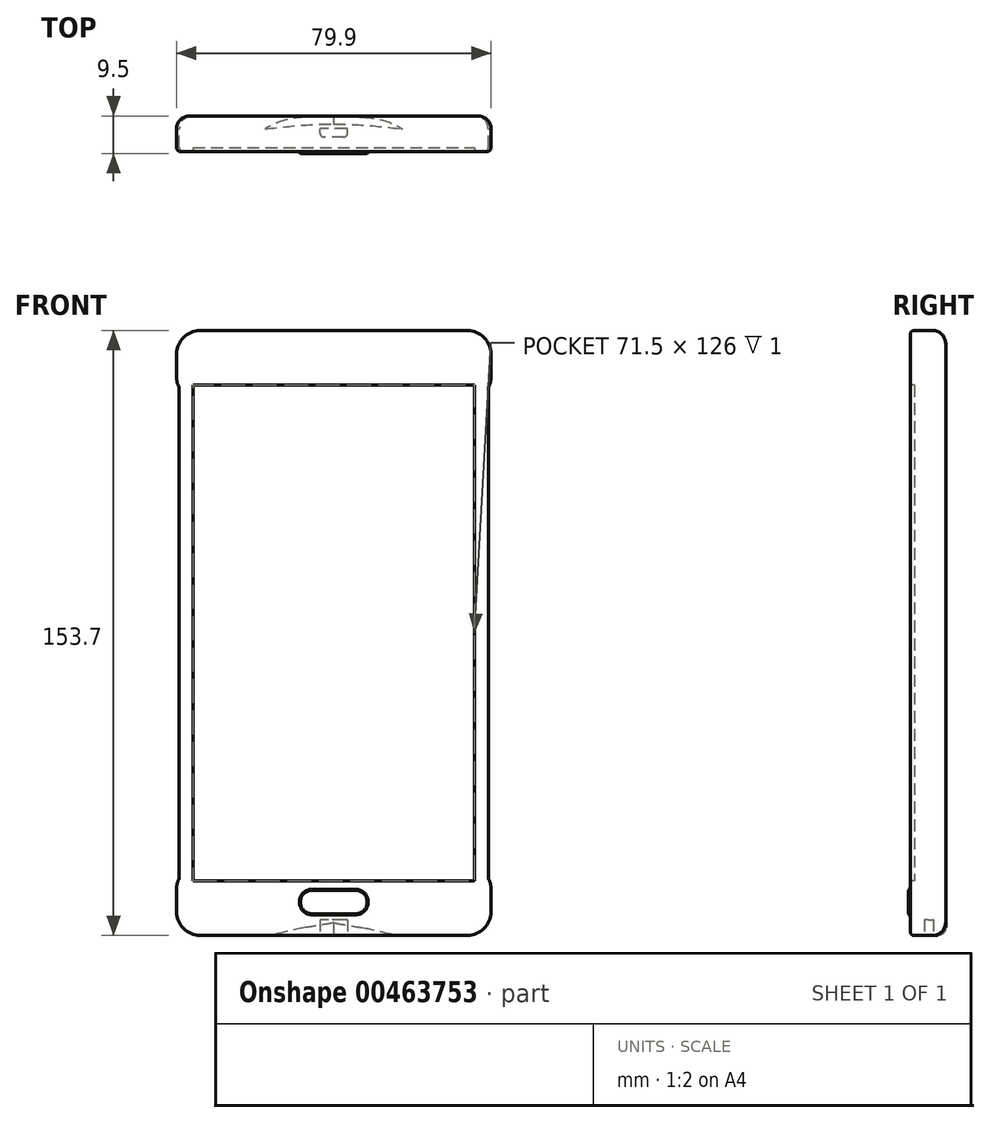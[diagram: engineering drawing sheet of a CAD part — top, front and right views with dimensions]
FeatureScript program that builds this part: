
annotation { "Feature Type Name" : "Feature", "Feature Type Description" : "" }
export const myFeature = defineFeature(function(context is Context, id is Id, definition is map)
    precondition{}
    {
        {
            var Q0;
            Q0=qCreatedBy(makeId("Front.planeOp"),FACE);
            var sketch = newSketch(context, id + "F0", { "sketchPlane" : qUnion([Q0])});
            skLineSegment(sketch, "E0.bottom", {"start": v(33.25, 76.85) * mm, "end": v(-33.25, 76.85) * mm});
            skLineSegment(sketch, "E0.top", {"start": v(33.95, -76.85) * mm, "end": v(-33.95, -76.85) * mm});
            skLineSegment(sketch, "E0.left", {"start": v(39.25, 61.9) * mm, "end": v(39.25, -61.9) * mm});
            skLineSegment(sketch, "E0.right", {"start": v(-39.25, 61.9) * mm, "end": v(-39.25, -61.9) * mm});
            skPoint(sketch, "E0.middle", {"position": v(0, 0) * mm});
            skLineSegment(sketch, "E1", {"start": v(0, 76.85) * mm, "end": v(0, -76.85) * mm, "construction": true});
            skLineSegment(sketch, "E2", {"start": v(-39.25, 0) * mm, "end": v(39.25, 0) * mm, "construction": true});
            skPoint(sketch, "E3.visualSharp", {"position": v(-39.25, 76.85) * mm});
            skPoint(sketch, "E4.visualSharp", {"position": v(39.25, 76.85) * mm});
            skPoint(sketch, "E5.visualSharp", {"position": v(39.25, -76.85) * mm});
            skPoint(sketch, "E6.visualSharp", {"position": v(-39.25, -76.85) * mm});
            skLineSegment(sketch, "E7.0", {"start": v(33.25, -62.85) * mm, "end": v(0, -62.85) * mm, "construction": true});
            skLineSegment(sketch, "E8.0", {"start": v(-39.95, -64.95) * mm, "end": v(-39.95, -70.85) * mm});
            skPoint(sketch, "E9.visualSharp", {"position": v(-39.95, -76.85) * mm});
            skArc(sketch, "E9.filletArc", {"start": v(-39.95, -70.85) * mm, "mid": v(-38.2, -75.1) * mm, "end": v(-33.95, -76.85) * mm});
            skPoint(sketch, "E10.visualSharp", {"position": v(-39.25, -62.85) * mm});
            skArc(sketch, "E10.filletArc", {"start": v(-39.45, -62.77) * mm, "mid": v(-39.3, -62.34) * mm, "end": v(-39.25, -61.9) * mm});
            skPoint(sketch, "E11.visualSharp", {"position": v(-39.95, -63.42) * mm});
            skArc(sketch, "E11.filletArc", {"start": v(-39.45, -62.77) * mm, "mid": v(-39.82, -63.83) * mm, "end": v(-39.95, -64.95) * mm});
            skArc(sketch, "E12.MirrorCS", {"start": v(39.45, -62.77) * mm, "mid": v(39.3, -62.34) * mm, "end": v(39.25, -61.9) * mm});
            skPoint(sketch, "E13.MirrorP", {"position": v(39.95, -63.42) * mm});
            skLineSegment(sketch, "E14.MirrorCS", {"start": v(39.95, -64.95) * mm, "end": v(39.95, -70.85) * mm});
            skArc(sketch, "E15.MirrorCS", {"start": v(39.95, -70.85) * mm, "mid": v(38.2, -75.1) * mm, "end": v(33.95, -76.85) * mm});
            skArc(sketch, "E16.MirrorCS", {"start": v(39.45, -62.77) * mm, "mid": v(39.82, -63.83) * mm, "end": v(39.95, -64.95) * mm});
            skArc(sketch, "E17.MirrorCS", {"start": v(39.45, 62.77) * mm, "mid": v(39.3, 62.34) * mm, "end": v(39.25, 61.9) * mm});
            skArc(sketch, "E18.MirrorCS", {"start": v(-39.45, 62.77) * mm, "mid": v(-39.3, 62.34) * mm, "end": v(-39.25, 61.9) * mm});
            skArc(sketch, "E19.MirrorCS", {"start": v(39.45, 62.77) * mm, "mid": v(39.82, 63.83) * mm, "end": v(39.95, 64.95) * mm});
            skArc(sketch, "E20.MirrorCS", {"start": v(-39.45, 62.77) * mm, "mid": v(-39.82, 63.83) * mm, "end": v(-39.95, 64.95) * mm});
            skArc(sketch, "E21.MirrorCS", {"start": v(39.95, 70.85) * mm, "mid": v(38.2, 75.1) * mm, "end": v(33.95, 76.85) * mm});
            skLineSegment(sketch, "E22.MirrorCS", {"start": v(39.95, 64.95) * mm, "end": v(39.95, 70.85) * mm});
            skArc(sketch, "E23.MirrorCS", {"start": v(-39.95, 70.85) * mm, "mid": v(-38.2, 75.1) * mm, "end": v(-33.95, 76.85) * mm});
            skLineSegment(sketch, "E24.MirrorCS", {"start": v(-39.95, 64.95) * mm, "end": v(-39.95, 70.85) * mm});
            skPoint(sketch, "E25.MirrorP", {"position": v(-39.95, 76.85) * mm});
            skPoint(sketch, "E26.MirrorP", {"position": v(-39.25, 62.85) * mm});
            skLineSegment(sketch, "E27.MirrorCS", {"start": v(33.25, 62.85) * mm, "end": v(0, 62.85) * mm, "construction": true});
            skPoint(sketch, "E28.MirrorP", {"position": v(-39.95, 63.42) * mm});
            skLineSegment(sketch, "E29.MirrorCS", {"start": v(33.95, 76.85) * mm, "end": v(-33.95, 76.85) * mm});
            skPoint(sketch, "E30.MirrorP", {"position": v(39.95, 63.42) * mm});
            skSolve(sketch);
        }
        {
            var Q0;
            Q0=makeQuery(id+"F0.imprint","IMPRINT",FACE,{"disambiguationData":[TD([[makeQuery(id+"F0.imprint","IMPRINT",EDGE,{"derivedFrom":sQuery(id+"F0.wireOp",EDGE,"E0.top")}),-1.0]])]});
            extrude(context, id + "F1", {"entities" : qUnion([Q0]), "depth" : 9 * mm});
        }
        {
            var Q0;
            Q0=makeQuery(id+"F1.opExtrude","CAP_FACE",FACE,{"disambiguationData":[OSD([sQuery(id+"F0.wireOp",EDGE,"E0.bottom"),sQuery(id+"F0.wireOp",EDGE,"E0.top"),sQuery(id+"F0.wireOp",EDGE,"E0.left"),sQuery(id+"F0.wireOp",EDGE,"E0.right"),sQuery(id+"F0.wireOp",EDGE,"E3.filletArc"),sQuery(id+"F0.wireOp",EDGE,"E4.filletArc"),sQuery(id+"F0.wireOp",EDGE,"E5.filletArc"),sQuery(id+"F0.wireOp",EDGE,"E6.filletArc")])],"isStart":false});
            var sketch = newSketch(context, id + "F2", { "sketchPlane" : qUnion([Q0])});
            skLineSegment(sketch, "E31.0", {"start": v(33.5, -68.35) * mm, "end": v(-33.5, -68.35) * mm, "construction": true});
            skLineSegment(sketch, "E32.0", {"start": v(0, 76.85) * mm, "end": v(0, -76.85) * mm, "construction": true});
            skLineSegment(sketch, "E33.bottom", {"start": v(5.5, -65.1) * mm, "end": v(-5.5, -65.1) * mm});
            skLineSegment(sketch, "E33.top", {"start": v(5.5, -71.6) * mm, "end": v(-5.5, -71.6) * mm});
            skLineSegment(sketch, "E33.left", {"start": v(8.75, -68.35) * mm, "end": v(8.75, -68.35) * mm});
            skLineSegment(sketch, "E33.right", {"start": v(-8.75, -68.35) * mm, "end": v(-8.75, -68.35) * mm});
            skPoint(sketch, "E33.middle", {"position": v(0, -68.35) * mm});
            skPoint(sketch, "E34.visualSharp", {"position": v(8.75, -65.1) * mm});
            skArc(sketch, "E34.filletArc", {"start": v(8.75, -68.35) * mm, "mid": v(7.8, -66.05) * mm, "end": v(5.5, -65.1) * mm});
            skPoint(sketch, "E35.visualSharp", {"position": v(8.75, -71.6) * mm});
            skArc(sketch, "E35.filletArc", {"start": v(5.5, -71.6) * mm, "mid": v(7.8, -70.65) * mm, "end": v(8.75, -68.35) * mm});
            skPoint(sketch, "E36.visualSharp", {"position": v(-8.75, -71.6) * mm});
            skArc(sketch, "E36.filletArc", {"start": v(-8.75, -68.35) * mm, "mid": v(-7.8, -70.65) * mm, "end": v(-5.5, -71.6) * mm});
            skPoint(sketch, "E37.visualSharp", {"position": v(-8.75, -65.1) * mm});
            skArc(sketch, "E37.filletArc", {"start": v(-5.5, -65.1) * mm, "mid": v(-7.8, -66.05) * mm, "end": v(-8.75, -68.35) * mm});
            skSolve(sketch);
        }
        {
            var Q0;
            Q0=makeQuery(id+"F2.imprint","IMPRINT",FACE,{"disambiguationData":[TD([[makeQuery(id+"F2.imprint","IMPRINT",EDGE,{"derivedFrom":sQuery(id+"F2.wireOp",EDGE,"E33.bottom")}),1.0]])]});
            extrude(context, id + "F3", {"entities" : qUnion([Q0]), "operationType" : NewBodyOperationType.ADD, "depth" : 0.5 * mm});
        }
        {
            var Q0;
            Q0=makeQuery(id+"F3.opExtrude","CAP_EDGE",EDGE,{"disambiguationData":[OSD([sQuery(id+"F2.wireOp",EDGE,"E33.bottom")])],"isStart":false});
            var Q1;
            Q1=makeQuery(id+"F3.opExtrude","CAP_EDGE",EDGE,{"disambiguationData":[OSD([sQuery(id+"F2.wireOp",EDGE,"E34.filletArc"),sQuery(id+"F2.wireOp",EDGE,"E35.filletArc")])],"isStart":false});
            var Q2;
            Q2=makeQuery(id+"F3.opExtrude","CAP_EDGE",EDGE,{"disambiguationData":[OSD([sQuery(id+"F2.wireOp",EDGE,"E33.top")])],"isStart":false});
            var Q3;
            Q3=makeQuery(id+"F3.opExtrude","CAP_EDGE",EDGE,{"disambiguationData":[OSD([sQuery(id+"F2.wireOp",EDGE,"E36.filletArc"),sQuery(id+"F2.wireOp",EDGE,"E37.filletArc")])],"isStart":false});
            chamfer(context, id + "F4", {"entities" : qUnion([Q0, Q1, Q2, Q3]), "width" : 0.25 * mm, "tangentPropagation" : true});
        }
        {
            var Q0;
            Q0=makeQuery(id+"F1.opExtrude","SWEPT_FACE",FACE,{"disambiguationData":[OSD([sQuery(id+"F0.wireOp",EDGE,"E0.top")])]});
            var sketch = newSketch(context, id + "F5", { "sketchPlane" : qUnion([Q0])});
            skLineSegment(sketch, "E38.0", {"start": v(33.95, 3.3) * mm, "end": v(-33.95, 3.3) * mm, "construction": true});
            skSolve(sketch);
        }
        {
            var Q0;
            Q0=makeQuery(id+"F1.opExtrude","CAP_EDGE",EDGE,{"disambiguationData":[OSD([sQuery(id+"F0.wireOp",EDGE,"E0.top")])],"isStart":true});
            fillet(context, id + "F6", {"entities" : qUnion([Q0]), "radius" : 3.3 * mm, "tangentPropagation" : true, "allowEdgeOverflow" : false});
        }
        {
            var Q0;
            Q0=makeQuery(id+"F1.opExtrude","CAP_EDGE",EDGE,{"disambiguationData":[OSD([sQuery(id+"F0.wireOp",EDGE,"E0.left")])],"isStart":false});
            var Q1;
            Q1=makeQuery(id+"F1.opExtrude","CAP_EDGE",EDGE,{"disambiguationData":[OSD([sQuery(id+"F0.wireOp",EDGE,"E0.top")])],"isStart":false});
            var Q2;
            Q2=makeQuery(id+"F1.opExtrude","CAP_EDGE",EDGE,{"disambiguationData":[OSD([sQuery(id+"F0.wireOp",EDGE,"E15.MirrorCS")])],"isStart":false});
            var Q3;
            Q3=makeQuery(id+"F1.opExtrude","CAP_EDGE",EDGE,{"disambiguationData":[OSD([sQuery(id+"F0.wireOp",EDGE,"E14.MirrorCS")])],"isStart":false});
            var Q4;
            Q4=makeQuery(id+"F1.opExtrude","CAP_EDGE",EDGE,{"disambiguationData":[OSD([sQuery(id+"F0.wireOp",EDGE,"E16.MirrorCS")])],"isStart":false});
            var Q5;
            Q5=makeQuery(id+"F1.opExtrude","CAP_EDGE",EDGE,{"disambiguationData":[OSD([sQuery(id+"F0.wireOp",EDGE,"E12.MirrorCS")])],"isStart":false});
            var Q6;
            Q6=makeQuery(id+"F1.opExtrude","CAP_EDGE",EDGE,{"disambiguationData":[OSD([sQuery(id+"F0.wireOp",EDGE,"E9.filletArc")])],"isStart":false});
            var Q7;
            Q7=makeQuery(id+"F1.opExtrude","CAP_EDGE",EDGE,{"disambiguationData":[OSD([sQuery(id+"F0.wireOp",EDGE,"E0.right")])],"isStart":false});
            var Q8;
            Q8=makeQuery(id+"F1.opExtrude","CAP_EDGE",EDGE,{"disambiguationData":[OSD([sQuery(id+"F0.wireOp",EDGE,"E10.filletArc")])],"isStart":false});
            var Q9;
            Q9=makeQuery(id+"F1.opExtrude","CAP_EDGE",EDGE,{"disambiguationData":[OSD([sQuery(id+"F0.wireOp",EDGE,"E8.0")])],"isStart":false});
            var Q10;
            Q10=makeQuery(id+"F1.opExtrude","CAP_EDGE",EDGE,{"disambiguationData":[OSD([sQuery(id+"F0.wireOp",EDGE,"E11.filletArc")])],"isStart":false});
            var Q11;
            Q11=makeQuery(id+"F1.opExtrude","CAP_FACE",FACE,{"disambiguationData":[OSD([sQuery(id+"F0.wireOp",EDGE,"E0.top"),sQuery(id+"F0.wireOp",EDGE,"E0.left"),sQuery(id+"F0.wireOp",EDGE,"E0.right"),sQuery(id+"F0.wireOp",EDGE,"E8.0"),sQuery(id+"F0.wireOp",EDGE,"E9.filletArc"),sQuery(id+"F0.wireOp",EDGE,"E10.filletArc"),sQuery(id+"F0.wireOp",EDGE,"E11.filletArc"),sQuery(id+"F0.wireOp",EDGE,"E12.MirrorCS"),sQuery(id+"F0.wireOp",EDGE,"E14.MirrorCS"),sQuery(id+"F0.wireOp",EDGE,"E15.MirrorCS"),sQuery(id+"F0.wireOp",EDGE,"E16.MirrorCS"),sQuery(id+"F0.wireOp",EDGE,"E17.MirrorCS"),sQuery(id+"F0.wireOp",EDGE,"E18.MirrorCS"),sQuery(id+"F0.wireOp",EDGE,"E19.MirrorCS"),sQuery(id+"F0.wireOp",EDGE,"E20.MirrorCS"),sQuery(id+"F0.wireOp",EDGE,"E21.MirrorCS"),sQuery(id+"F0.wireOp",EDGE,"E22.MirrorCS"),sQuery(id+"F0.wireOp",EDGE,"E23.MirrorCS"),sQuery(id+"F0.wireOp",EDGE,"E24.MirrorCS"),sQuery(id+"F0.wireOp",EDGE,"E29.MirrorCS")])],"isStart":false});
            fillet(context, id + "F7", {"entities" : qUnion([Q0, Q1, Q2, Q3, Q4, Q5, Q6, Q7, Q8, Q9, Q10, Q11]), "radius" : 1 * mm, "tangentPropagation" : true, "allowEdgeOverflow" : false});
        }
        {
            var Q0;
            {var subQ0=sQuery(id+"F0.wireOp",EDGE,"E0.top");Q0=makeQuery(id+"F5.imprint","IMPRINT",FACE,{"disambiguationData":[TD([[makeQuery(id+"F5.imprint","IMPRINT",EDGE,{"derivedFrom":makeQuery(id+"F1.opExtrude","CAP_EDGE",EDGE,{"disambiguationData":[OSD([subQ0])],"isStart":true})}),-1.0]])]});}
            var sketch = newSketch(context, id + "F8", { "sketchPlane" : qUnion([Q0])});
            skLineSegment(sketch, "E39.0.0", {"start": v(-33.95, 0) * mm, "end": v(33.95, 0) * mm});
            skLineSegment(sketch, "E39.0.1", {"start": v(33.95, 0) * mm, "end": v(33.95, 9) * mm});
            skLineSegment(sketch, "E39.0.2", {"start": v(33.95, 9) * mm, "end": v(-33.95, 9) * mm});
            skLineSegment(sketch, "E39.0.3", {"start": v(-33.95, 9) * mm, "end": v(-33.95, 0) * mm});
            skLineSegment(sketch, "E40", {"start": v(0, 0) * mm, "end": v(0, 21.42) * mm, "construction": true});
            skLineSegment(sketch, "E41.0", {"start": v(12.75, 0.1) * mm, "end": v(12.75, 21.42) * mm, "construction": true});
            skFitSpline(sketch, "E42", {"points": [v(0, 0) * mm, v(33.95, 3.34) * mm], "startDerivative": vector(38.25, 0.27) * mm, "endDerivative": vector(33.95, 3.34) * mm});
            skFitSpline(sketch, "E43.MirrorCS", {"points": [v(0, 0) * mm, v(-33.95, 3.34) * mm], "startDerivative": vector(-38.25, 0.27) * mm, "endDerivative": vector(-33.95, 3.34) * mm});
            skLineSegment(sketch, "E44", {"start": v(-33.95, 3.34) * mm, "end": v(33.95, 3.34) * mm});
            skSolve(sketch);
        }
        {
            var Q0;
            Q0=makeQuery(id+"F8.imprint","IMPRINT",FACE,{"disambiguationData":[TD([[makeQuery(id+"F8.imprint","IMPRINT",EDGE,{"derivedFrom":sQuery(id+"F8.wireOp",EDGE,"E42")}),1.0]])]});
            var Q1;
            Q1=sQuery(id+"F8.wireOp",EDGE,"E43.MirrorCS");
            var Q2;
            Q2=sQuery(id+"F8.wireOp",EDGE,"E42");
            var Q3;
            Q3=sQuery(id+"F8.wireOp",EDGE,"E44");
            var Q4;
            Q4=sQuery(id+"F8.wireOp",VERTEX,"E43.MirrorCS.start");
            extrude(context, id + "F9", {"entities" : qUnion([Q0]), "operationType" : NewBodyOperationType.ADD, "surfaceEntities" : qUnion([Q1, Q2, Q3]), "oppositeDirection" : true, "endBoundEntityVertex" : qUnion([Q4]), "depth" : 25 * mm});
        }
        {
            var Q0;
            Q0=makeQuery(id+"F9.opExtrude","CAP_EDGE",EDGE,{"disambiguationData":[OSD([sQuery(id+"F8.wireOp",EDGE,"E43.MirrorCS")])],"isStart":true});
            var Q1;
            Q1=makeQuery(id+"F9.opExtrude","CAP_EDGE",EDGE,{"disambiguationData":[OSD([sQuery(id+"F8.wireOp",EDGE,"E42")])],"isStart":true});
            fillet(context, id + "F10", {"entities" : qUnion([Q0, Q1]), "radius" : 2 * mm, "tangentPropagation" : true, "allowEdgeOverflow" : false});
        }
        {
            var Q0;
            Q0=makeQuery(id+"F1.opExtrude","CAP_FACE",FACE,{"disambiguationData":[OSD([sQuery(id+"F0.wireOp",EDGE,"E0.top"),sQuery(id+"F0.wireOp",EDGE,"E0.left"),sQuery(id+"F0.wireOp",EDGE,"E0.right"),sQuery(id+"F0.wireOp",EDGE,"E8.0"),sQuery(id+"F0.wireOp",EDGE,"E9.filletArc"),sQuery(id+"F0.wireOp",EDGE,"E10.filletArc"),sQuery(id+"F0.wireOp",EDGE,"E11.filletArc"),sQuery(id+"F0.wireOp",EDGE,"E12.MirrorCS"),sQuery(id+"F0.wireOp",EDGE,"E14.MirrorCS"),sQuery(id+"F0.wireOp",EDGE,"E15.MirrorCS"),sQuery(id+"F0.wireOp",EDGE,"E16.MirrorCS"),sQuery(id+"F0.wireOp",EDGE,"E17.MirrorCS"),sQuery(id+"F0.wireOp",EDGE,"E18.MirrorCS"),sQuery(id+"F0.wireOp",EDGE,"E19.MirrorCS"),sQuery(id+"F0.wireOp",EDGE,"E20.MirrorCS"),sQuery(id+"F0.wireOp",EDGE,"E21.MirrorCS"),sQuery(id+"F0.wireOp",EDGE,"E22.MirrorCS"),sQuery(id+"F0.wireOp",EDGE,"E23.MirrorCS"),sQuery(id+"F0.wireOp",EDGE,"E24.MirrorCS"),sQuery(id+"F0.wireOp",EDGE,"E29.MirrorCS")])],"isStart":false});
            var sketch = newSketch(context, id + "F11", { "sketchPlane" : qUnion([Q0])});
            skLineSegment(sketch, "E45.0", {"start": v(0, 76.85) * mm, "end": v(0, -76.85) * mm});
            skLineSegment(sketch, "E46.0", {"start": v(-39.25, 0) * mm, "end": v(39.25, 0) * mm});
            skLineSegment(sketch, "E47.bottom", {"start": v(-35.75, 63) * mm, "end": v(35.75, 63) * mm});
            skLineSegment(sketch, "E47.top", {"start": v(-35.75, -63) * mm, "end": v(35.75, -63) * mm});
            skLineSegment(sketch, "E47.left", {"start": v(-35.75, 63) * mm, "end": v(-35.75, -63) * mm});
            skLineSegment(sketch, "E47.right", {"start": v(35.75, 63) * mm, "end": v(35.75, -63) * mm});
            skPoint(sketch, "E47.middle", {"position": v(0, 0) * mm});
            skSolve(sketch);
        }
        {
            var Q0;
            {var subQ0=sQuery(id+"F11.wireOp",EDGE,"E47.bottom");var subQ1=sQuery(id+"F11.wireOp",EDGE,"E45.0");var subQ2=makeQuery(id+"F11.imprint","INTERSECT",VERTEX,{"derivedFrom":[subQ1,subQ0]});Q0=makeQuery(id+"F11.imprint","IMPRINT",FACE,{"disambiguationData":[TD([[makeQuery(id+"F11.imprint","IMPRINT",EDGE,{"disambiguationData":[TD([[subQ2,-1.0]])],"derivedFrom":subQ1}),-1.0]])]});}
            var Q1;
            {var subQ0=sQuery(id+"F11.wireOp",EDGE,"E46.0");var subQ1=sQuery(id+"F11.wireOp",EDGE,"E45.0");var subQ2=makeQuery(id+"F11.imprint","INTERSECT",VERTEX,{"derivedFrom":[subQ1,subQ0]});Q1=makeQuery(id+"F11.imprint","IMPRINT",FACE,{"disambiguationData":[TD([[makeQuery(id+"F11.imprint","IMPRINT",EDGE,{"disambiguationData":[TD([[subQ2,-1.0]])],"derivedFrom":subQ1}),-1.0]])]});}
            var Q2;
            {var subQ0=sQuery(id+"F11.wireOp",EDGE,"E46.0");var subQ1=sQuery(id+"F11.wireOp",EDGE,"E45.0");var subQ2=makeQuery(id+"F11.imprint","INTERSECT",VERTEX,{"derivedFrom":[subQ1,subQ0]});Q2=makeQuery(id+"F11.imprint","IMPRINT",FACE,{"disambiguationData":[TD([[makeQuery(id+"F11.imprint","IMPRINT",EDGE,{"disambiguationData":[TD([[subQ2,-1.0]])],"derivedFrom":subQ1}),1.0]])]});}
            var Q3;
            {var subQ0=sQuery(id+"F11.wireOp",EDGE,"E47.bottom");var subQ1=sQuery(id+"F11.wireOp",EDGE,"E45.0");var subQ2=makeQuery(id+"F11.imprint","INTERSECT",VERTEX,{"derivedFrom":[subQ1,subQ0]});Q3=makeQuery(id+"F11.imprint","IMPRINT",FACE,{"disambiguationData":[TD([[makeQuery(id+"F11.imprint","IMPRINT",EDGE,{"disambiguationData":[TD([[subQ2,-1.0]])],"derivedFrom":subQ1}),1.0]])]});}
            extrude(context, id + "F12", {"entities" : qUnion([Q0, Q1, Q2, Q3]), "operationType" : NewBodyOperationType.REMOVE, "oppositeDirection" : true, "depth" : 1 * mm});
        }
        {
            var Q0;
            {var subQ0=sQuery(id+"F8.wireOp",EDGE,"E39.0.2");Q0=makeQuery(id+"F8.imprint","IMPRINT",FACE,{"disambiguationData":[TD([[makeQuery(id+"F8.imprint","IMPRINT",EDGE,{"derivedFrom":subQ0}),1.0]])]});}
            var sketch = newSketch(context, id + "F13", { "sketchPlane" : qUnion([Q0])});
            skLineSegment(sketch, "E48.0", {"start": v(0, 0) * mm, "end": v(0, 21.42) * mm, "construction": true});
            skLineSegment(sketch, "E49.0", {"start": v(33.95, 9) * mm, "end": v(-33.95, 9) * mm});
            skLineSegment(sketch, "E50.0", {"start": v(33.95, 4.23) * mm, "end": v(-33.95, 4.23) * mm, "construction": true});
            skLineSegment(sketch, "E51.bottom", {"start": v(2.5, 5.33) * mm, "end": v(-2.5, 5.33) * mm});
            skLineSegment(sketch, "E51.top", {"start": v(3.25, 3.13) * mm, "end": v(-3.25, 3.13) * mm});
            skLineSegment(sketch, "E51.left", {"start": v(3.5, 4.33) * mm, "end": v(3.5, 3.38) * mm});
            skLineSegment(sketch, "E51.right", {"start": v(-3.5, 4.33) * mm, "end": v(-3.5, 3.38) * mm});
            skPoint(sketch, "E51.middle", {"position": v(0, 4.23) * mm});
            skPoint(sketch, "E52.visualSharp", {"position": v(-3.5, 5.33) * mm});
            skArc(sketch, "E52.filletArc", {"start": v(-2.5, 5.33) * mm, "mid": v(-3.2, 5.04) * mm, "end": v(-3.5, 4.33) * mm});
            skPoint(sketch, "E53.visualSharp", {"position": v(3.5, 5.33) * mm});
            skArc(sketch, "E53.filletArc", {"start": v(3.5, 4.33) * mm, "mid": v(3.2, 5.04) * mm, "end": v(2.5, 5.33) * mm});
            skPoint(sketch, "E54.visualSharp", {"position": v(-3.5, 3.13) * mm});
            skArc(sketch, "E54.filletArc", {"start": v(-3.5, 3.38) * mm, "mid": v(-3.43, 3.2) * mm, "end": v(-3.25, 3.13) * mm});
            skPoint(sketch, "E55.visualSharp", {"position": v(3.5, 3.13) * mm});
            skArc(sketch, "E55.filletArc", {"start": v(3.25, 3.13) * mm, "mid": v(3.43, 3.2) * mm, "end": v(3.5, 3.38) * mm});
            skSolve(sketch);
        }
        {
            var Q0;
            Q0 = qSketchRegion(id + "F13", true);
            extrude(context, id + "F14", {"entities" : qUnion([Q0]), "operationType" : NewBodyOperationType.REMOVE, "oppositeDirection" : true, "depth" : 4 * mm});
        }
    });
